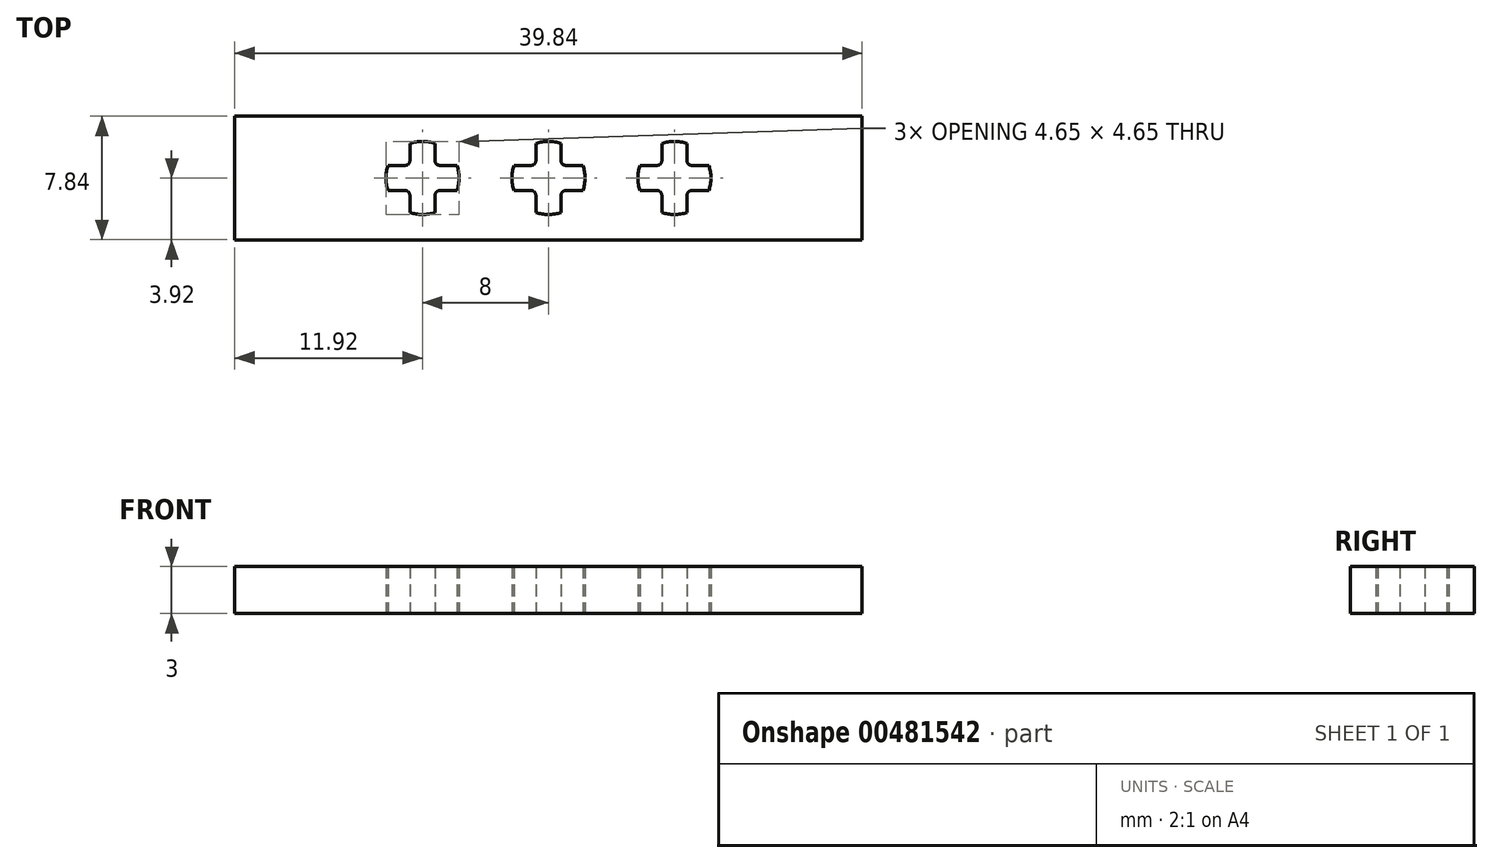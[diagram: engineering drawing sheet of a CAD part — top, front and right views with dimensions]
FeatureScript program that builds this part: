
annotation { "Feature Type Name" : "Feature", "Feature Type Description" : "" }
export const myFeature = defineFeature(function(context is Context, id is Id, definition is map)
    precondition{}
    {
        {
            var Q0;
            Q0=qCreatedBy(makeId("Top.planeOp"),FACE);
            var sketch = newSketch(context, id + "F0", { "sketchPlane" : qUnion([Q0])});
            skLineSegment(sketch, "E0.bottom", {"start": v(-20, 4) * mm, "end": v(20, 4) * mm, "construction": true});
            skLineSegment(sketch, "E0.top", {"start": v(-20, -4) * mm, "end": v(20, -4) * mm, "construction": true});
            skLineSegment(sketch, "E0.left", {"start": v(-20, 4) * mm, "end": v(-20, -4) * mm, "construction": true});
            skLineSegment(sketch, "E0.right", {"start": v(20, 4) * mm, "end": v(20, -4) * mm, "construction": true});
            skLineSegment(sketch, "E1", {"start": v(-16.8, 2.18) * mm, "end": v(-15.2, 2.18) * mm, "construction": true});
            skLineSegment(sketch, "E2", {"start": v(-15.2, 2.18) * mm, "end": v(-15.2, 1.1) * mm});
            skLineSegment(sketch, "E3", {"start": v(-14.9, 0.8) * mm, "end": v(-13.82, 0.8) * mm});
            skLineSegment(sketch, "E4", {"start": v(-13.82, 0.8) * mm, "end": v(-16, 0) * mm, "construction": true});
            skLineSegment(sketch, "E5", {"start": v(-16, 0) * mm, "end": v(-16.8, 2.18) * mm, "construction": true});
            skArc(sketch, "E6", {"start": v(-15.2, 2.18) * mm, "mid": v(-16, 2.33) * mm, "end": v(-16.8, 2.18) * mm});
            skArc(sketch, "E7", {"start": v(-15.2, 1.1) * mm, "mid": v(-15.11, 0.89) * mm, "end": v(-14.9, 0.8) * mm});
            skLineSegment(sketch, "E8", {"start": v(-15.2, 2.18) * mm, "end": v(-15.2, 0.8) * mm, "construction": true});
            skLineSegment(sketch, "E9", {"start": v(-15.2, 0.8) * mm, "end": v(-13.82, 0.8) * mm, "construction": true});
            skArc(sketch, "E10.1.0", {"start": v(-18.18, 0.8) * mm, "mid": v(-18.32, 0) * mm, "end": v(-18.18, -0.8) * mm});
            skArc(sketch, "E10.1.1", {"start": v(-17.1, 0.8) * mm, "mid": v(-16.89, 0.89) * mm, "end": v(-16.8, 1.1) * mm});
            skLineSegment(sketch, "E10.1.2", {"start": v(-18.18, 0.8) * mm, "end": v(-17.1, 0.8) * mm});
            skLineSegment(sketch, "E10.1.3", {"start": v(-16.8, 1.1) * mm, "end": v(-16.8, 2.18) * mm});
            skArc(sketch, "E10.2.0", {"start": v(-16.8, -2.18) * mm, "mid": v(-16, -2.32) * mm, "end": v(-15.2, -2.18) * mm});
            skArc(sketch, "E10.2.1", {"start": v(-16.8, -1.1) * mm, "mid": v(-16.89, -0.89) * mm, "end": v(-17.1, -0.8) * mm});
            skLineSegment(sketch, "E10.2.2", {"start": v(-16.8, -2.18) * mm, "end": v(-16.8, -1.1) * mm});
            skLineSegment(sketch, "E10.2.3", {"start": v(-17.1, -0.8) * mm, "end": v(-18.18, -0.8) * mm});
            skArc(sketch, "E10.3.0", {"start": v(-13.82, -0.8) * mm, "mid": v(-13.67, 0) * mm, "end": v(-13.82, 0.8) * mm});
            skArc(sketch, "E10.3.1", {"start": v(-14.9, -0.8) * mm, "mid": v(-15.11, -0.89) * mm, "end": v(-15.2, -1.1) * mm});
            skLineSegment(sketch, "E10.3.2", {"start": v(-13.82, -0.8) * mm, "end": v(-14.9, -0.8) * mm});
            skLineSegment(sketch, "E10.3.3", {"start": v(-15.2, -1.1) * mm, "end": v(-15.2, -2.18) * mm});
            skArc(sketch, "E11.1.0.0", {"start": v(-7.2, 2.18) * mm, "mid": v(-8, 2.33) * mm, "end": v(-8.8, 2.18) * mm});
            skArc(sketch, "E11.1.0.1", {"start": v(-6.9, -0.8) * mm, "mid": v(-7.11, -0.89) * mm, "end": v(-7.2, -1.1) * mm});
            skLineSegment(sketch, "E11.1.0.2", {"start": v(-5.82, -0.8) * mm, "end": v(-6.9, -0.8) * mm});
            skLineSegment(sketch, "E11.1.0.3", {"start": v(-9.1, -0.8) * mm, "end": v(-10.18, -0.8) * mm});
            skArc(sketch, "E11.1.0.4", {"start": v(-8.8, -1.1) * mm, "mid": v(-8.89, -0.89) * mm, "end": v(-9.1, -0.8) * mm});
            skLineSegment(sketch, "E11.1.0.5", {"start": v(-8.8, 1.1) * mm, "end": v(-8.8, 2.18) * mm});
            skLineSegment(sketch, "E11.1.0.6", {"start": v(-10.18, 0.8) * mm, "end": v(-9.1, 0.8) * mm});
            skArc(sketch, "E11.1.0.7", {"start": v(-9.1, 0.8) * mm, "mid": v(-8.89, 0.89) * mm, "end": v(-8.8, 1.1) * mm});
            skArc(sketch, "E11.1.0.8", {"start": v(-8.8, -2.18) * mm, "mid": v(-8, -2.32) * mm, "end": v(-7.2, -2.18) * mm});
            skArc(sketch, "E11.1.0.9", {"start": v(-10.18, 0.8) * mm, "mid": v(-10.32, 0) * mm, "end": v(-10.18, -0.8) * mm});
            skPoint(sketch, "E11.1.0.10", {"position": v(-8, 0) * mm});
            skLineSegment(sketch, "E11.1.0.11", {"start": v(-8.8, -2.18) * mm, "end": v(-8.8, -1.1) * mm});
            skArc(sketch, "E11.1.0.12", {"start": v(-5.82, -0.8) * mm, "mid": v(-5.67, 0) * mm, "end": v(-5.82, 0.8) * mm});
            skLineSegment(sketch, "E11.1.0.13", {"start": v(-7.2, -1.1) * mm, "end": v(-7.2, -2.18) * mm});
            skLineSegment(sketch, "E11.1.0.14", {"start": v(-7.2, 2.18) * mm, "end": v(-7.2, 1.1) * mm});
            skLineSegment(sketch, "E11.1.0.15", {"start": v(-6.9, 0.8) * mm, "end": v(-5.82, 0.8) * mm});
            skArc(sketch, "E11.1.0.16", {"start": v(-7.2, 1.1) * mm, "mid": v(-7.11, 0.89) * mm, "end": v(-6.9, 0.8) * mm});
            skArc(sketch, "E11.2.0.0", {"start": v(0.8, 2.18) * mm, "mid": v(0, 2.33) * mm, "end": v(-0.8, 2.18) * mm});
            skArc(sketch, "E11.2.0.1", {"start": v(1.1, -0.8) * mm, "mid": v(0.89, -0.89) * mm, "end": v(0.8, -1.1) * mm});
            skLineSegment(sketch, "E11.2.0.2", {"start": v(2.18, -0.8) * mm, "end": v(1.1, -0.8) * mm});
            skLineSegment(sketch, "E11.2.0.3", {"start": v(-1.1, -0.8) * mm, "end": v(-2.18, -0.8) * mm});
            skArc(sketch, "E11.2.0.4", {"start": v(-0.8, -1.1) * mm, "mid": v(-0.89, -0.89) * mm, "end": v(-1.1, -0.8) * mm});
            skLineSegment(sketch, "E11.2.0.5", {"start": v(-0.8, 1.1) * mm, "end": v(-0.8, 2.18) * mm});
            skLineSegment(sketch, "E11.2.0.6", {"start": v(-2.18, 0.8) * mm, "end": v(-1.1, 0.8) * mm});
            skArc(sketch, "E11.2.0.7", {"start": v(-1.1, 0.8) * mm, "mid": v(-0.89, 0.89) * mm, "end": v(-0.8, 1.1) * mm});
            skArc(sketch, "E11.2.0.8", {"start": v(-0.8, -2.18) * mm, "mid": v(0, -2.32) * mm, "end": v(0.8, -2.18) * mm});
            skArc(sketch, "E11.2.0.9", {"start": v(-2.18, 0.8) * mm, "mid": v(-2.32, 0) * mm, "end": v(-2.18, -0.8) * mm});
            skPoint(sketch, "E11.2.0.10", {"position": v(0, 0) * mm});
            skLineSegment(sketch, "E11.2.0.11", {"start": v(-0.8, -2.18) * mm, "end": v(-0.8, -1.1) * mm});
            skArc(sketch, "E11.2.0.12", {"start": v(2.18, -0.8) * mm, "mid": v(2.33, 0) * mm, "end": v(2.18, 0.8) * mm});
            skLineSegment(sketch, "E11.2.0.13", {"start": v(0.8, -1.1) * mm, "end": v(0.8, -2.18) * mm});
            skLineSegment(sketch, "E11.2.0.14", {"start": v(0.8, 2.18) * mm, "end": v(0.8, 1.1) * mm});
            skLineSegment(sketch, "E11.2.0.15", {"start": v(1.1, 0.8) * mm, "end": v(2.18, 0.8) * mm});
            skArc(sketch, "E11.2.0.16", {"start": v(0.8, 1.1) * mm, "mid": v(0.89, 0.89) * mm, "end": v(1.1, 0.8) * mm});
            skLineSegment(sketch, "E11.direction1", {"start": v(-16.8, -2.18) * mm, "end": v(-8.8, -2.18) * mm, "construction": true});
            skLineSegment(sketch, "E11.direction2", {"start": v(-16.8, -2.18) * mm, "end": v(-16.8, -10.18) * mm, "construction": true});
            skLineSegment(sketch, "E12.bottom", {"start": v(-19.92, 3.93) * mm, "end": v(19.93, 3.93) * mm});
            skLineSegment(sketch, "E12.top", {"start": v(-19.92, -3.92) * mm, "end": v(19.93, -3.92) * mm});
            skLineSegment(sketch, "E12.left", {"start": v(-19.92, 3.93) * mm, "end": v(-19.92, -3.92) * mm});
            skLineSegment(sketch, "E12.right", {"start": v(19.93, 3.92) * mm, "end": v(19.93, -3.92) * mm});
            skArc(sketch, "E13.0.3.0", {"start": v(8.8, 2.18) * mm, "mid": v(8, 2.33) * mm, "end": v(7.2, 2.18) * mm});
            skArc(sketch, "E13.4.3.0", {"start": v(9.1, -0.8) * mm, "mid": v(8.89, -0.89) * mm, "end": v(8.8, -1.1) * mm});
            skLineSegment(sketch, "E13.8.3.0", {"start": v(10.18, -0.8) * mm, "end": v(9.1, -0.8) * mm});
            skLineSegment(sketch, "E13.11.3.0", {"start": v(6.9, -0.8) * mm, "end": v(5.82, -0.8) * mm});
            skArc(sketch, "E13.14.3.0", {"start": v(7.2, -1.1) * mm, "mid": v(7.11, -0.89) * mm, "end": v(6.9, -0.8) * mm});
            skLineSegment(sketch, "E13.18.3.0", {"start": v(7.2, 1.1) * mm, "end": v(7.2, 2.18) * mm});
            skLineSegment(sketch, "E13.21.3.0", {"start": v(5.82, 0.8) * mm, "end": v(6.9, 0.8) * mm});
            skArc(sketch, "E13.24.3.0", {"start": v(6.9, 0.8) * mm, "mid": v(7.11, 0.89) * mm, "end": v(7.2, 1.1) * mm});
            skArc(sketch, "E13.28.3.0", {"start": v(7.2, -2.18) * mm, "mid": v(8, -2.32) * mm, "end": v(8.8, -2.18) * mm});
            skArc(sketch, "E13.32.3.0", {"start": v(5.82, 0.8) * mm, "mid": v(5.68, 0) * mm, "end": v(5.82, -0.8) * mm});
            skPoint(sketch, "E13.36.3.0", {"position": v(8, 0) * mm});
            skLineSegment(sketch, "E13.37.3.0", {"start": v(7.2, -2.18) * mm, "end": v(7.2, -1.1) * mm});
            skArc(sketch, "E13.40.3.0", {"start": v(10.18, -0.8) * mm, "mid": v(10.33, 0) * mm, "end": v(10.18, 0.8) * mm});
            skLineSegment(sketch, "E13.44.3.0", {"start": v(8.8, -1.1) * mm, "end": v(8.8, -2.18) * mm});
            skLineSegment(sketch, "E13.47.3.0", {"start": v(8.8, 2.18) * mm, "end": v(8.8, 1.1) * mm});
            skLineSegment(sketch, "E13.50.3.0", {"start": v(9.1, 0.8) * mm, "end": v(10.18, 0.8) * mm});
            skArc(sketch, "E13.53.3.0", {"start": v(8.8, 1.1) * mm, "mid": v(8.89, 0.89) * mm, "end": v(9.1, 0.8) * mm});
            skArc(sketch, "E14.0.4.0", {"start": v(16.8, 2.18) * mm, "mid": v(16, 2.33) * mm, "end": v(15.2, 2.18) * mm});
            skArc(sketch, "E14.4.4.0", {"start": v(17.1, -0.8) * mm, "mid": v(16.89, -0.89) * mm, "end": v(16.8, -1.1) * mm});
            skLineSegment(sketch, "E14.8.4.0", {"start": v(18.18, -0.8) * mm, "end": v(17.1, -0.8) * mm});
            skLineSegment(sketch, "E14.11.4.0", {"start": v(14.9, -0.8) * mm, "end": v(13.82, -0.8) * mm});
            skArc(sketch, "E14.14.4.0", {"start": v(15.2, -1.1) * mm, "mid": v(15.11, -0.89) * mm, "end": v(14.9, -0.8) * mm});
            skLineSegment(sketch, "E14.18.4.0", {"start": v(15.2, 1.1) * mm, "end": v(15.2, 2.18) * mm});
            skLineSegment(sketch, "E14.21.4.0", {"start": v(13.82, 0.8) * mm, "end": v(14.9, 0.8) * mm});
            skArc(sketch, "E14.24.4.0", {"start": v(14.9, 0.8) * mm, "mid": v(15.11, 0.89) * mm, "end": v(15.2, 1.1) * mm});
            skArc(sketch, "E14.28.4.0", {"start": v(15.2, -2.18) * mm, "mid": v(16, -2.32) * mm, "end": v(16.8, -2.18) * mm});
            skArc(sketch, "E14.32.4.0", {"start": v(13.82, 0.8) * mm, "mid": v(13.68, 0) * mm, "end": v(13.82, -0.8) * mm});
            skPoint(sketch, "E14.36.4.0", {"position": v(16, 0) * mm});
            skLineSegment(sketch, "E14.37.4.0", {"start": v(15.2, -2.18) * mm, "end": v(15.2, -1.1) * mm});
            skArc(sketch, "E14.40.4.0", {"start": v(18.18, -0.8) * mm, "mid": v(18.33, 0) * mm, "end": v(18.18, 0.8) * mm});
            skLineSegment(sketch, "E14.44.4.0", {"start": v(16.8, -1.1) * mm, "end": v(16.8, -2.18) * mm});
            skLineSegment(sketch, "E14.47.4.0", {"start": v(16.8, 2.18) * mm, "end": v(16.8, 1.1) * mm});
            skLineSegment(sketch, "E14.50.4.0", {"start": v(17.1, 0.8) * mm, "end": v(18.18, 0.8) * mm});
            skArc(sketch, "E14.53.4.0", {"start": v(16.8, 1.1) * mm, "mid": v(16.89, 0.89) * mm, "end": v(17.1, 0.8) * mm});
            skSolve(sketch);
        }
        {
            var Q0;
            Q0=makeQuery(id+"F0.imprint","IMPRINT",FACE,{"disambiguationData":[TD([[makeQuery(id+"F0.imprint","IMPRINT",EDGE,{"derivedFrom":sQuery(id+"F0.wireOp",EDGE,"E2")}),-1.0]])]});
            var Q1;
            Q1=makeQuery(id+"F0.imprint","IMPRINT",FACE,{"disambiguationData":[TD([[makeQuery(id+"F0.imprint","IMPRINT",EDGE,{"derivedFrom":sQuery(id+"F0.wireOp",EDGE,"E14.0.4.0")}),1.0]])]});
            var Q2;
            Q2=makeQuery(id+"F0.imprint","IMPRINT",FACE,{"disambiguationData":[TD([[makeQuery(id+"F0.imprint","IMPRINT",EDGE,{"derivedFrom":sQuery(id+"F0.wireOp",EDGE,"E2")}),1.0]])]});
            extrude(context, id + "F1", {"entities" : qUnion([Q0, Q1, Q2]), "depth" : 3 * mm, "offsetDistance" : 25 * mm});
        }
    });
